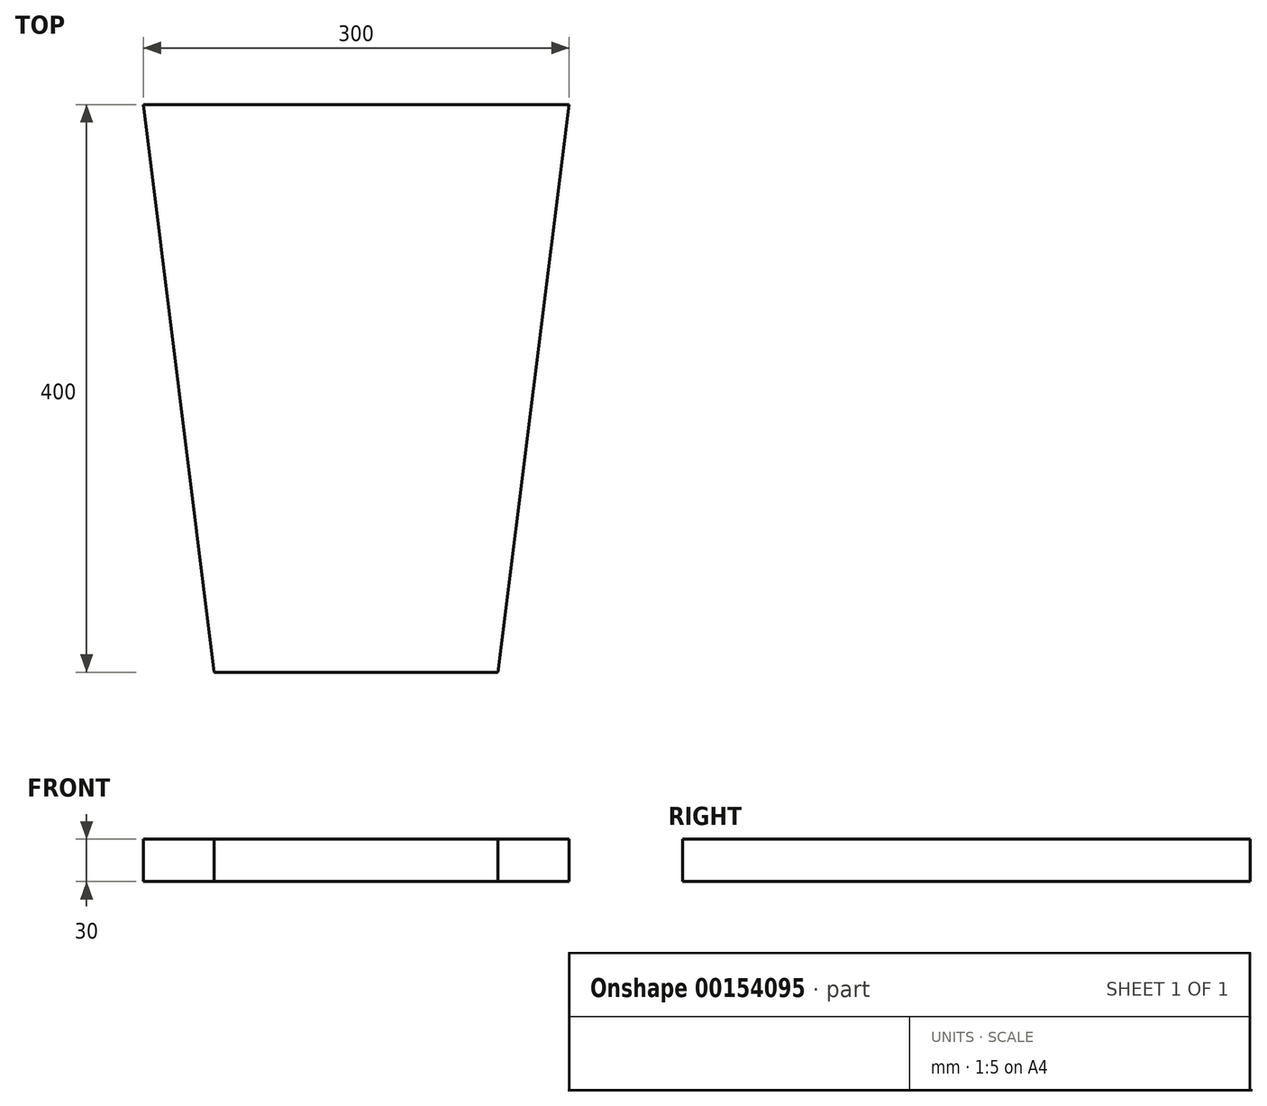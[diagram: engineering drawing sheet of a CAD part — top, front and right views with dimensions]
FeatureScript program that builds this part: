
annotation { "Feature Type Name" : "Feature", "Feature Type Description" : "" }
export const myFeature = defineFeature(function(context is Context, id is Id, definition is map)
    precondition{}
    {
        {
            var Q0;
            Q0=qCreatedBy(makeId("Top.planeOp"),FACE);
            var sketch = newSketch(context, id + "F0", { "sketchPlane" : qUnion([Q0])});
            skLineSegment(sketch, "E0.bottom", {"start": v(-150, 200) * mm, "end": v(150, 200) * mm});
            skPoint(sketch, "E0.middle", {"position": v(0, 0) * mm});
            skLineSegment(sketch, "E1", {"start": v(-100, -200) * mm, "end": v(100, -200) * mm});
            skLineSegment(sketch, "E2", {"start": v(-150, 200) * mm, "end": v(-100, -200) * mm});
            skLineSegment(sketch, "E3", {"start": v(100, -200) * mm, "end": v(150, 200) * mm});
            skSolve(sketch);
        }
        {
            var Q0;
            Q0=makeQuery(id+"F0.imprint","IMPRINT",FACE,{"disambiguationData":[TD([[makeQuery(id+"F0.imprint","IMPRINT",EDGE,{"derivedFrom":sQuery(id+"F0.wireOp",EDGE,"E0.bottom")}),-1.0]])]});
            extrude(context, id + "F1", {"entities" : qUnion([Q0]), "depth" : 30 * mm});
        }
    });
